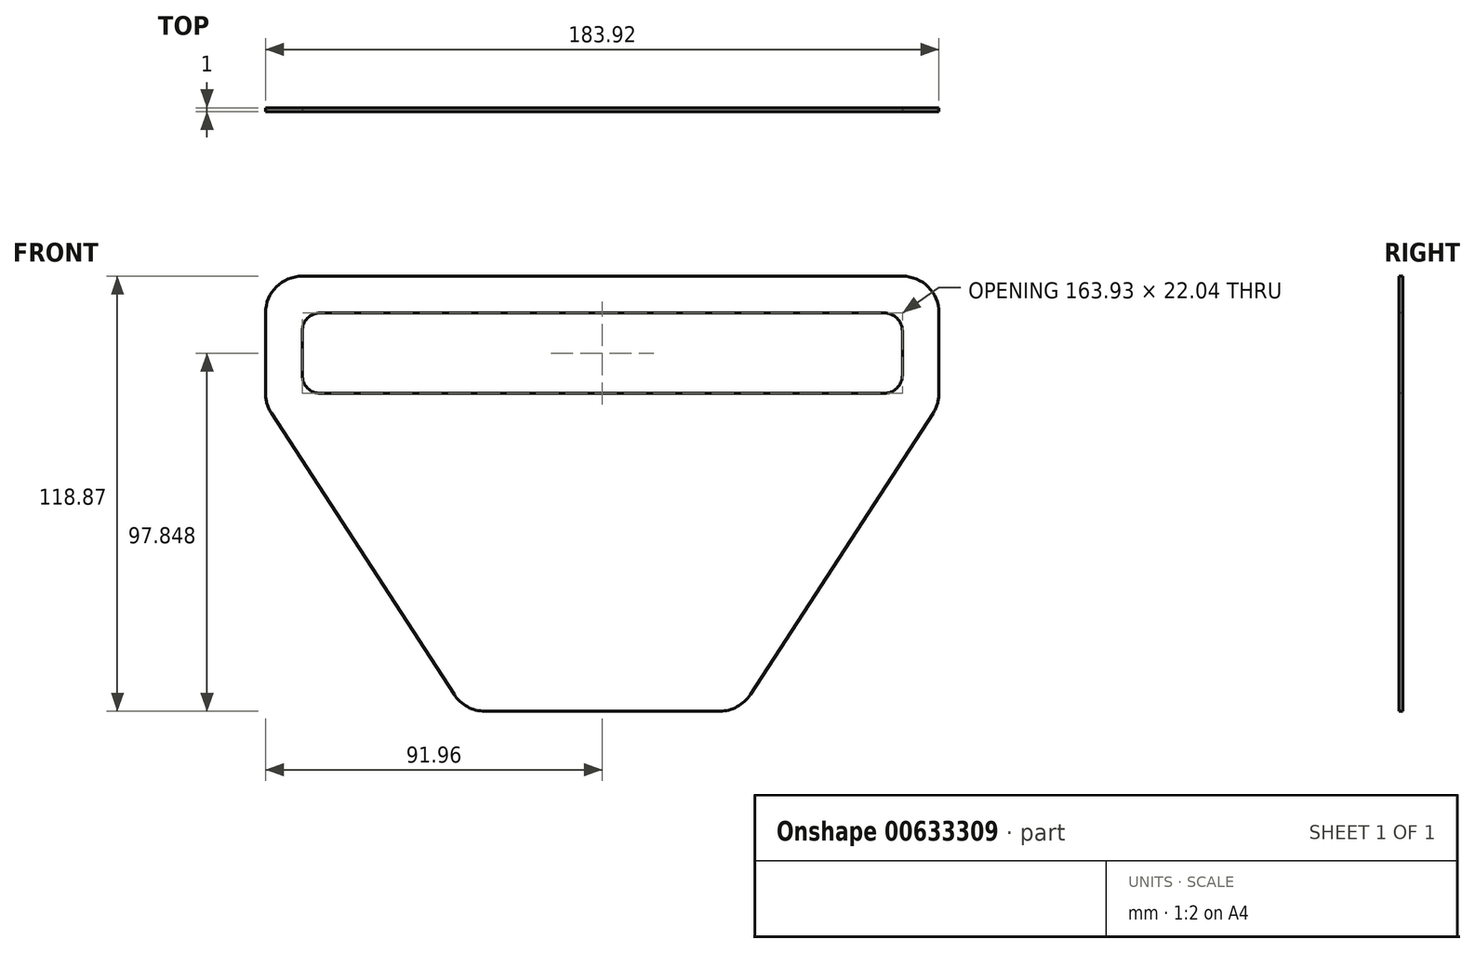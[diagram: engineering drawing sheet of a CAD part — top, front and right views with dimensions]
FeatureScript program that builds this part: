
annotation { "Feature Type Name" : "Feature", "Feature Type Description" : "" }
export const myFeature = defineFeature(function(context is Context, id is Id, definition is map)
    precondition{}
    {
        {
            var Q0;
            Q0=qCreatedBy(makeId("Front.planeOp"),FACE);
            var sketch = newSketch(context, id + "F0", { "sketchPlane" : qUnion([Q0])});
            skLineSegment(sketch, "E0", {"start": v(0, 0) * mm, "end": v(32.07, 0) * mm});
            skLineSegment(sketch, "E1", {"start": v(40.46, 4.55) * mm, "end": v(90.35, 81.38) * mm});
            skPoint(sketch, "E2.visualSharp", {"position": v(37.5, 0) * mm});
            skArc(sketch, "E2.filletArc", {"start": v(32.07, 0) * mm, "mid": v(36.84, 1.21) * mm, "end": v(40.46, 4.55) * mm});
            skLineSegment(sketch, "E3.MirrorCS", {"start": v(-40.46, 4.55) * mm, "end": v(-90.35, 81.38) * mm});
            skPoint(sketch, "E4.MirrorP", {"position": v(-37.5, 0) * mm});
            skLineSegment(sketch, "E5.MirrorCS", {"start": v(0, 0) * mm, "end": v(-32.07, 0) * mm});
            skArc(sketch, "E6.MirrorCS", {"start": v(-32.07, 0) * mm, "mid": v(-36.84, 1.21) * mm, "end": v(-40.46, 4.55) * mm});
            skLineSegment(sketch, "E7.top", {"start": v(-81.96, 118.87) * mm, "end": v(81.96, 118.87) * mm});
            skLineSegment(sketch, "E7.left", {"start": v(-91.96, 86.83) * mm, "end": v(-91.96, 108.87) * mm});
            skLineSegment(sketch, "E7.right", {"start": v(91.96, 86.83) * mm, "end": v(91.96, 108.87) * mm});
            skPoint(sketch, "E8.visualSharp", {"position": v(-91.96, 118.87) * mm});
            skArc(sketch, "E8.filletArc", {"start": v(-81.96, 118.87) * mm, "mid": v(-89.03, 115.94) * mm, "end": v(-91.96, 108.87) * mm});
            skPoint(sketch, "E9.visualSharp", {"position": v(91.96, 118.87) * mm});
            skArc(sketch, "E9.filletArc", {"start": v(91.96, 108.87) * mm, "mid": v(89.03, 115.94) * mm, "end": v(81.96, 118.87) * mm});
            skPoint(sketch, "E10.visualSharp", {"position": v(-91.96, 83.87) * mm});
            skArc(sketch, "E10.filletArc", {"start": v(-91.96, 86.83) * mm, "mid": v(-91.55, 83.99) * mm, "end": v(-90.35, 81.38) * mm});
            skPoint(sketch, "E11.visualSharp", {"position": v(91.96, 83.87) * mm});
            skArc(sketch, "E11.filletArc", {"start": v(90.35, 81.38) * mm, "mid": v(91.55, 83.99) * mm, "end": v(91.96, 86.83) * mm});
            skSolve(sketch);
        }
        {
            var Q0;
            Q0 = qSketchRegion(id + "F0", true);
            extrude(context, id + "F1", {"entities" : qUnion([Q0]), "depth" : 1 * mm, "offsetDistance" : 25 * mm});
        }
        {
            var Q0;
            Q0=makeQuery(id+"F1.opExtrude","SWEPT_BODY",BODY,{"disambiguationData":[OSD([sQuery(id+"F0.wireOp",EDGE,"E0"),sQuery(id+"F0.wireOp",EDGE,"E1"),sQuery(id+"F0.wireOp",EDGE,"E2.filletArc"),sQuery(id+"F0.wireOp",EDGE,"E3.MirrorCS"),sQuery(id+"F0.wireOp",EDGE,"E5.MirrorCS"),sQuery(id+"F0.wireOp",EDGE,"E6.MirrorCS"),sQuery(id+"F0.wireOp",EDGE,"E7.top"),sQuery(id+"F0.wireOp",EDGE,"E7.left"),sQuery(id+"F0.wireOp",EDGE,"E7.right"),sQuery(id+"F0.wireOp",EDGE,"E8.filletArc"),sQuery(id+"F0.wireOp",EDGE,"E9.filletArc"),sQuery(id+"F0.wireOp",EDGE,"E10.filletArc"),sQuery(id+"F0.wireOp",EDGE,"E11.filletArc")])]});
            transform(context, id + "F2", {"entities" : qUnion([Q0]), "transformType" : TransformType.TRANSLATION_3D, "dx" : 0 * mm, "dy" : 0 * mm, "dz" : 0 * mm, "makeCopy" : true});
        }
        {
            var Q0;
            Q0=makeQuery(id+"F1.opExtrude","CAP_FACE",FACE,{"disambiguationData":[OSD([sQuery(id+"F0.wireOp",EDGE,"E0"),sQuery(id+"F0.wireOp",EDGE,"E1"),sQuery(id+"F0.wireOp",EDGE,"E2.filletArc"),sQuery(id+"F0.wireOp",EDGE,"E3.MirrorCS"),sQuery(id+"F0.wireOp",EDGE,"E5.MirrorCS"),sQuery(id+"F0.wireOp",EDGE,"E6.MirrorCS"),sQuery(id+"F0.wireOp",EDGE,"E7.top"),sQuery(id+"F0.wireOp",EDGE,"E7.left"),sQuery(id+"F0.wireOp",EDGE,"E7.right"),sQuery(id+"F0.wireOp",EDGE,"E8.filletArc"),sQuery(id+"F0.wireOp",EDGE,"E9.filletArc"),sQuery(id+"F0.wireOp",EDGE,"E10.filletArc"),sQuery(id+"F0.wireOp",EDGE,"E11.filletArc")])],"isStart":false});
            var sketch = newSketch(context, id + "F3", { "sketchPlane" : qUnion([Q0])});
            skLineSegment(sketch, "E12.bottom", {"start": v(-76.96, 108.87) * mm, "end": v(76.96, 108.87) * mm});
            skLineSegment(sketch, "E12.top", {"start": v(-76.96, 86.83) * mm, "end": v(76.96, 86.83) * mm});
            skLineSegment(sketch, "E12.left", {"start": v(-81.96, 103.87) * mm, "end": v(-81.96, 91.83) * mm});
            skLineSegment(sketch, "E12.right", {"start": v(81.96, 103.87) * mm, "end": v(81.96, 91.83) * mm});
            skPoint(sketch, "E13.visualSharp", {"position": v(-81.96, 108.87) * mm});
            skArc(sketch, "E13.filletArc", {"start": v(-76.96, 108.87) * mm, "mid": v(-80.5, 107.4) * mm, "end": v(-81.96, 103.87) * mm});
            skPoint(sketch, "E14.visualSharp", {"position": v(-81.96, 86.83) * mm});
            skArc(sketch, "E14.filletArc", {"start": v(-81.96, 91.83) * mm, "mid": v(-80.5, 88.3) * mm, "end": v(-76.96, 86.83) * mm});
            skPoint(sketch, "E15.visualSharp", {"position": v(81.96, 108.87) * mm});
            skArc(sketch, "E15.filletArc", {"start": v(81.96, 103.87) * mm, "mid": v(80.5, 107.4) * mm, "end": v(76.96, 108.87) * mm});
            skPoint(sketch, "E16.visualSharp", {"position": v(81.96, 86.83) * mm});
            skArc(sketch, "E16.filletArc", {"start": v(76.96, 86.83) * mm, "mid": v(80.5, 88.3) * mm, "end": v(81.96, 91.83) * mm});
            skSolve(sketch);
        }
        {
            var Q0;
            Q0 = qSketchRegion(id + "F3", true);
            extrude(context, id + "F4", {"entities" : qUnion([Q0]), "operationType" : NewBodyOperationType.REMOVE, "oppositeDirection" : true, "depth" : 25 * mm, "offsetDistance" : 25 * mm});
        }
        {
            var Q0;
            Q0=makeQuery(id+"F2.opPattern","COPY",BODY,{"derivedFrom":makeQuery(id+"F1.opExtrude","SWEPT_BODY",BODY,{"disambiguationData":[OSD([sQuery(id+"F0.wireOp",EDGE,"E0"),sQuery(id+"F0.wireOp",EDGE,"E1"),sQuery(id+"F0.wireOp",EDGE,"E2.filletArc"),sQuery(id+"F0.wireOp",EDGE,"E3.MirrorCS"),sQuery(id+"F0.wireOp",EDGE,"E5.MirrorCS"),sQuery(id+"F0.wireOp",EDGE,"E6.MirrorCS"),sQuery(id+"F0.wireOp",EDGE,"E7.top"),sQuery(id+"F0.wireOp",EDGE,"E7.left"),sQuery(id+"F0.wireOp",EDGE,"E7.right"),sQuery(id+"F0.wireOp",EDGE,"E8.filletArc"),sQuery(id+"F0.wireOp",EDGE,"E9.filletArc"),sQuery(id+"F0.wireOp",EDGE,"E10.filletArc"),sQuery(id+"F0.wireOp",EDGE,"E11.filletArc")])]}),"instanceName":"1"});
            deleteBodies(context, id + "F5", {"entities" : qUnion([Q0])});
        }
    });
